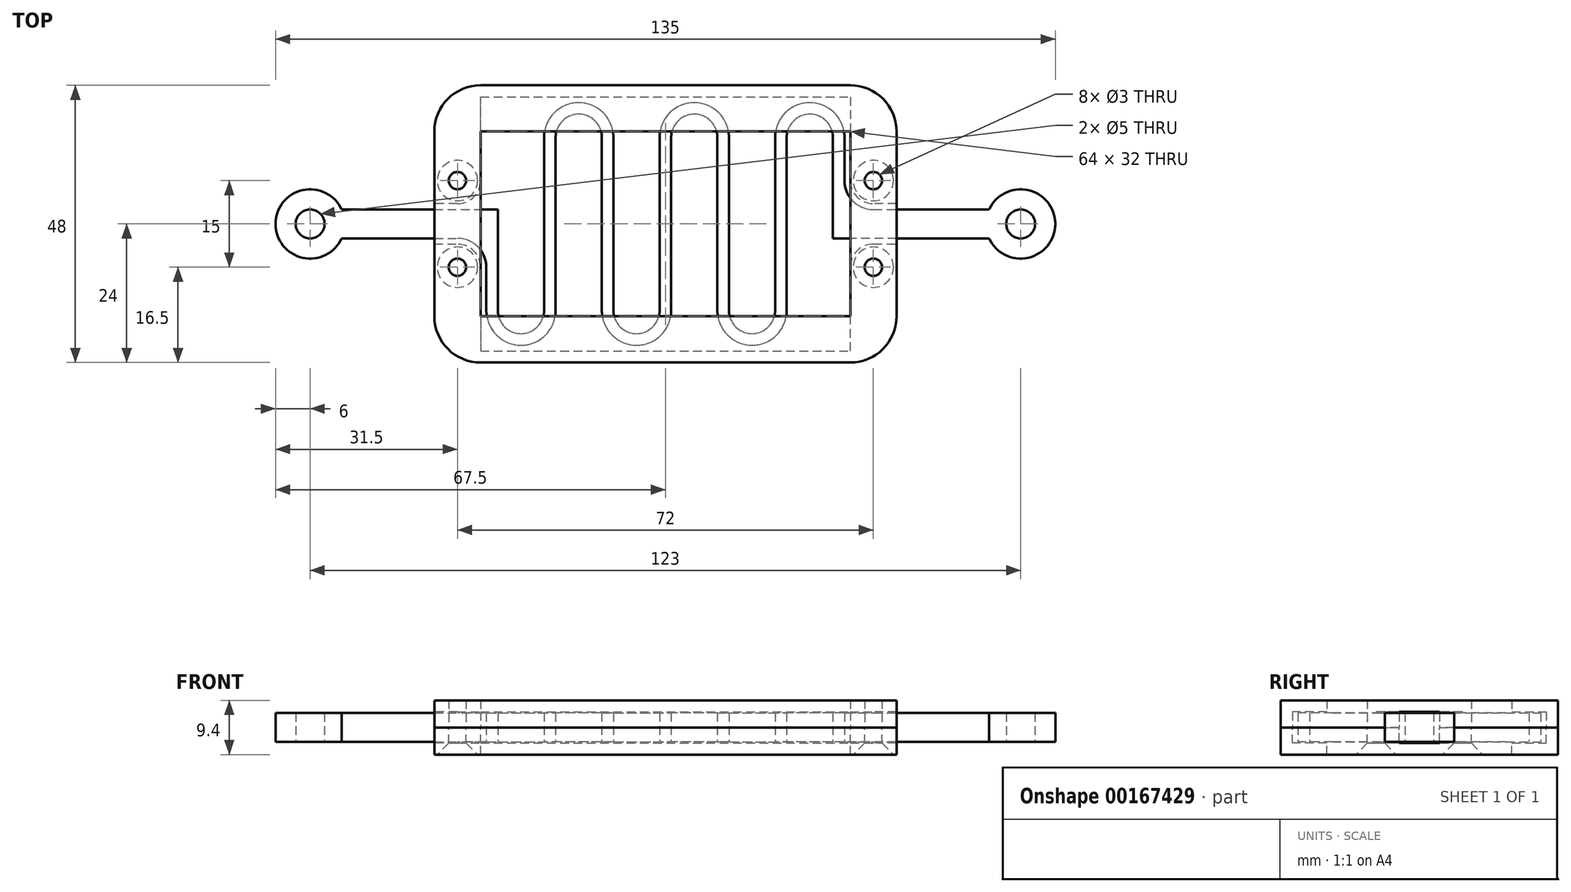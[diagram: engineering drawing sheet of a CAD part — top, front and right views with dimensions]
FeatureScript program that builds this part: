
annotation { "Feature Type Name" : "Feature", "Feature Type Description" : "" }
export const myFeature = defineFeature(function(context is Context, id is Id, definition is map)
    precondition{}
    {
        {
            var Q0;
            Q0=qCreatedBy(makeId("Top.planeOp"),FACE);
            var sketch = newSketch(context, id + "F0", { "sketchPlane" : qUnion([Q0])});
            skLineSegment(sketch, "E0", {"start": v(0, -15) * mm, "end": v(0, 15) * mm, "construction": true});
            skArc(sketch, "E1", {"start": v(10, 15) * mm, "mid": v(5, 20) * mm, "end": v(0, 15) * mm, "construction": true});
            skArc(sketch, "E2", {"start": v(-10, -15) * mm, "mid": v(-5, -20) * mm, "end": v(0, -15) * mm, "construction": true});
            skLineSegment(sketch, "E3", {"start": v(10, 15) * mm, "end": v(10, -15) * mm, "construction": true});
            skLineSegment(sketch, "E4.1.0.0", {"start": v(20, -15) * mm, "end": v(20, 15) * mm, "construction": true});
            skArc(sketch, "E4.1.0.1", {"start": v(10, -15) * mm, "mid": v(15, -20) * mm, "end": v(20, -15) * mm, "construction": true});
            skArc(sketch, "E4.1.0.2", {"start": v(30, 15) * mm, "mid": v(25, 20) * mm, "end": v(20, 15) * mm, "construction": true});
            skLineSegment(sketch, "E4.1.0.3", {"start": v(30, 15) * mm, "end": v(30, -15) * mm, "construction": true});
            skLineSegment(sketch, "E4.2.0.0", {"start": v(40, -15) * mm, "end": v(40, 15) * mm, "construction": true});
            skArc(sketch, "E4.2.0.1", {"start": v(30, -15) * mm, "mid": v(35, -20) * mm, "end": v(40, -15) * mm, "construction": true});
            skArc(sketch, "E4.2.0.2", {"start": v(50, 15) * mm, "mid": v(45, 20) * mm, "end": v(40, 15) * mm, "construction": true});
            skLineSegment(sketch, "E4.2.0.3", {"start": v(50, 15) * mm, "end": v(50, -15) * mm, "construction": true});
            skLineSegment(sketch, "E4.direction1", {"start": v(-10, -15) * mm, "end": v(10, -15) * mm, "construction": true});
            skLineSegment(sketch, "E5.bottom", {"start": v(-39, 2.5) * mm, "end": v(-9, 2.5) * mm, "construction": true});
            skLineSegment(sketch, "E5.top", {"start": v(-39, -2.5) * mm, "end": v(-16, -2.5) * mm, "construction": true});
            skLineSegment(sketch, "E5.left", {"start": v(-39, 2.5) * mm, "end": v(-39, -2.5) * mm, "construction": true});
            skLineSegment(sketch, "E5.right", {"start": v(-9, 2.5) * mm, "end": v(-9, -2.5) * mm});
            skLineSegment(sketch, "E6.top", {"start": v(49, -2.5) * mm, "end": v(79, -2.5) * mm, "construction": true});
            skLineSegment(sketch, "E6.left", {"start": v(49, 2.5) * mm, "end": v(49, -2.5) * mm});
            skLineSegment(sketch, "E6.right", {"start": v(79, 2.5) * mm, "end": v(79, -2.5) * mm, "construction": true});
            skPoint(sketch, "E7", {"position": v(-9, 0) * mm});
            skLineSegment(sketch, "E8.0", {"start": v(49, 15) * mm, "end": v(49, -2.5) * mm});
            skArc(sketch, "E8.1", {"start": v(49, 15) * mm, "mid": v(45, 19) * mm, "end": v(41, 15) * mm});
            skLineSegment(sketch, "E8.2", {"start": v(9, 15) * mm, "end": v(9, -15) * mm});
            skArc(sketch, "E8.3", {"start": v(9, 15) * mm, "mid": v(5, 19) * mm, "end": v(1, 15) * mm});
            skLineSegment(sketch, "E8.4", {"start": v(1, -15) * mm, "end": v(1, 15) * mm});
            skArc(sketch, "E8.5", {"start": v(-11, -15) * mm, "mid": v(-5, -21) * mm, "end": v(1, -15) * mm});
            skArc(sketch, "E8.6", {"start": v(9, -15) * mm, "mid": v(15, -21) * mm, "end": v(21, -15) * mm});
            skLineSegment(sketch, "E8.7", {"start": v(21, -15) * mm, "end": v(21, 15) * mm});
            skArc(sketch, "E8.8", {"start": v(29, 15) * mm, "mid": v(25, 19) * mm, "end": v(21, 15) * mm});
            skLineSegment(sketch, "E8.9", {"start": v(29, 15) * mm, "end": v(29, -15) * mm});
            skArc(sketch, "E8.10", {"start": v(29, -15) * mm, "mid": v(35, -21) * mm, "end": v(41, -15) * mm});
            skLineSegment(sketch, "E8.11", {"start": v(41, -15) * mm, "end": v(41, 15) * mm});
            skLineSegment(sketch, "E9.0", {"start": v(51, 15) * mm, "end": v(51, 7.5) * mm});
            skArc(sketch, "E9.1", {"start": v(51, 15) * mm, "mid": v(45, 21) * mm, "end": v(39, 15) * mm});
            skLineSegment(sketch, "E9.2", {"start": v(11, 15) * mm, "end": v(11, -15) * mm});
            skArc(sketch, "E9.3", {"start": v(11, 15) * mm, "mid": v(5, 21) * mm, "end": v(-1, 15) * mm});
            skLineSegment(sketch, "E9.4", {"start": v(-1, -15) * mm, "end": v(-1, 15) * mm});
            skArc(sketch, "E9.5", {"start": v(-9, -15) * mm, "mid": v(-5, -19) * mm, "end": v(-1, -15) * mm});
            skArc(sketch, "E9.6", {"start": v(11, -15) * mm, "mid": v(15, -19) * mm, "end": v(19, -15) * mm});
            skLineSegment(sketch, "E9.7", {"start": v(19, -15) * mm, "end": v(19, 15) * mm});
            skArc(sketch, "E9.8", {"start": v(31, 15) * mm, "mid": v(25, 21) * mm, "end": v(19, 15) * mm});
            skLineSegment(sketch, "E9.9", {"start": v(31, 15) * mm, "end": v(31, -15) * mm});
            skArc(sketch, "E9.10", {"start": v(31, -15) * mm, "mid": v(35, -19) * mm, "end": v(39, -15) * mm});
            skLineSegment(sketch, "E9.11", {"start": v(39, -15) * mm, "end": v(39, 15) * mm});
            skLineSegment(sketch, "E10", {"start": v(-11, -15) * mm, "end": v(-11, -7.5) * mm});
            skLineSegment(sketch, "E11", {"start": v(-9, -2.5) * mm, "end": v(-9, -15) * mm});
            skLineSegment(sketch, "E12.trimOffspring", {"start": v(56, 2.5) * mm, "end": v(79, 2.5) * mm, "construction": true});
            skPoint(sketch, "E13.visualSharp", {"position": v(-11, -2.5) * mm});
            skArc(sketch, "E13.filletArc", {"start": v(-11, -7.5) * mm, "mid": v(-12.46, -3.96) * mm, "end": v(-16, -2.5) * mm});
            skPoint(sketch, "E14.visualSharp", {"position": v(51, 2.5) * mm});
            skArc(sketch, "E14.filletArc", {"start": v(51, 7.5) * mm, "mid": v(52.46, 3.96) * mm, "end": v(56, 2.5) * mm});
            skCircle(sketch, "E15", {"center": v(-41.5, 0) * mm, "radius": 2.5 * mm});
            skArc(sketch, "E16", {"start": v(-36.05, 2.5) * mm, "mid": v(-47.5, 0) * mm, "end": v(-36.05, -2.5) * mm});
            skLineSegment(sketch, "E17", {"start": v(-36.05, 2.5) * mm, "end": v(-9, 2.5) * mm});
            skLineSegment(sketch, "E18", {"start": v(-36.05, -2.5) * mm, "end": v(-16, -2.5) * mm});
            skCircle(sketch, "E19", {"center": v(81.5, 0) * mm, "radius": 2.5 * mm});
            skArc(sketch, "E20", {"start": v(76.05, -2.5) * mm, "mid": v(87.5, 0) * mm, "end": v(76.05, 2.5) * mm});
            skLineSegment(sketch, "E21", {"start": v(56, 2.5) * mm, "end": v(76.05, 2.5) * mm});
            skLineSegment(sketch, "E22", {"start": v(76.05, -2.5) * mm, "end": v(49, -2.5) * mm});
            skSolve(sketch);
        }
        {
            var Q0;
            Q0 = qSketchRegion(id + "F0", true);
            extrude(context, id + "F1", {"entities" : qUnion([Q0]), "endBound" : BoundingType.SYMMETRIC, "depth" : 5 * mm});
        }
        {
            var Q0;
            Q0=qCreatedBy(makeId("Top.planeOp"),FACE);
            var sketch = newSketch(context, id + "F2", { "sketchPlane" : qUnion([Q0])});
            skLineSegment(sketch, "E23.bottom", {"start": v(-16, -7.5) * mm, "end": v(56, -7.5) * mm, "construction": true});
            skLineSegment(sketch, "E23.top", {"start": v(-16, 7.5) * mm, "end": v(56, 7.5) * mm, "construction": true});
            skLineSegment(sketch, "E23.left", {"start": v(-16, -7.5) * mm, "end": v(-16, 7.5) * mm, "construction": true});
            skLineSegment(sketch, "E23.right", {"start": v(56, -7.5) * mm, "end": v(56, 7.5) * mm, "construction": true});
            skCircle(sketch, "E24", {"center": v(-16, 7.5) * mm, "radius": 4 * mm, "construction": true});
            skCircle(sketch, "E25", {"center": v(-16, -7.5) * mm, "radius": 4 * mm, "construction": true});
            skCircle(sketch, "E26", {"center": v(56, -7.5) * mm, "radius": 4 * mm, "construction": true});
            skCircle(sketch, "E27", {"center": v(56, 7.5) * mm, "radius": 4 * mm, "construction": true});
            skLineSegment(sketch, "E28", {"start": v(-12, 7.5) * mm, "end": v(-12, 22) * mm});
            skLineSegment(sketch, "E29", {"start": v(-12, 22) * mm, "end": v(52, 22) * mm});
            skLineSegment(sketch, "E30", {"start": v(52, 22) * mm, "end": v(52, 7.5) * mm});
            skArc(sketch, "E31", {"start": v(-16, 3.5) * mm, "mid": v(-13.17, 4.67) * mm, "end": v(-12, 7.5) * mm});
            skArc(sketch, "E32", {"start": v(-12, -7.5) * mm, "mid": v(-13.17, -4.67) * mm, "end": v(-16, -3.5) * mm});
            skArc(sketch, "E33", {"start": v(52, 7.5) * mm, "mid": v(53.17, 4.67) * mm, "end": v(56, 3.5) * mm});
            skArc(sketch, "E34", {"start": v(56, -3.5) * mm, "mid": v(53.17, -4.67) * mm, "end": v(52, -7.5) * mm});
            skLineSegment(sketch, "E35", {"start": v(-12, -7.5) * mm, "end": v(-12, -22) * mm});
            skLineSegment(sketch, "E36", {"start": v(-12, -22) * mm, "end": v(52, -22) * mm});
            skLineSegment(sketch, "E37", {"start": v(52, -22) * mm, "end": v(52, -7.5) * mm});
            skLineSegment(sketch, "E38", {"start": v(-16, 3.5) * mm, "end": v(-20, 3.5) * mm});
            skLineSegment(sketch, "E39", {"start": v(-20, 3.5) * mm, "end": v(-20, 16) * mm});
            skLineSegment(sketch, "E40", {"start": v(-12, 24) * mm, "end": v(52, 24) * mm});
            skLineSegment(sketch, "E41", {"start": v(60, 16) * mm, "end": v(60, 3.5) * mm});
            skLineSegment(sketch, "E42", {"start": v(60, 3.5) * mm, "end": v(56, 3.5) * mm});
            skLineSegment(sketch, "E43", {"start": v(56, -3.5) * mm, "end": v(60, -3.5) * mm});
            skLineSegment(sketch, "E44", {"start": v(60, -3.5) * mm, "end": v(60, -16) * mm});
            skLineSegment(sketch, "E45", {"start": v(52, -24) * mm, "end": v(-12, -24) * mm});
            skLineSegment(sketch, "E46", {"start": v(-20, -16) * mm, "end": v(-20, -3.5) * mm});
            skLineSegment(sketch, "E47", {"start": v(-20, -3.5) * mm, "end": v(-16, -3.5) * mm});
            skPoint(sketch, "E48.visualSharp", {"position": v(-20, 24) * mm});
            skArc(sketch, "E48.filletArc", {"start": v(-12, 24) * mm, "mid": v(-17.66, 21.66) * mm, "end": v(-20, 16) * mm});
            skPoint(sketch, "E49.visualSharp", {"position": v(60, 24) * mm});
            skArc(sketch, "E49.filletArc", {"start": v(60, 16) * mm, "mid": v(57.66, 21.66) * mm, "end": v(52, 24) * mm});
            skPoint(sketch, "E50.visualSharp", {"position": v(60, -24) * mm});
            skArc(sketch, "E50.filletArc", {"start": v(52, -24) * mm, "mid": v(57.66, -21.66) * mm, "end": v(60, -16) * mm});
            skPoint(sketch, "E51.visualSharp", {"position": v(-20, -24) * mm});
            skArc(sketch, "E51.filletArc", {"start": v(-20, -16) * mm, "mid": v(-17.66, -21.66) * mm, "end": v(-12, -24) * mm});
            skCircle(sketch, "E52", {"center": v(-16, 7.5) * mm, "radius": 1.5 * mm});
            skCircle(sketch, "E53", {"center": v(-16, -7.5) * mm, "radius": 1.5 * mm});
            skCircle(sketch, "E54", {"center": v(56, 7.5) * mm, "radius": 1.5 * mm});
            skCircle(sketch, "E55", {"center": v(56, -7.5) * mm, "radius": 1.5 * mm});
            skSolve(sketch);
        }
        {
            var Q0;
            Q0=makeQuery(id+"F2.imprint","IMPRINT",FACE,{"disambiguationData":[TD([[makeQuery(id+"F2.imprint","IMPRINT",EDGE,{"derivedFrom":sQuery(id+"F2.wireOp",EDGE,"E28")}),1.0]])]});
            var Q1;
            Q1=makeQuery(id+"F2.imprint","IMPRINT",FACE,{"disambiguationData":[TD([[makeQuery(id+"F2.imprint","IMPRINT",EDGE,{"derivedFrom":sQuery(id+"F2.wireOp",EDGE,"E32")}),1.0]])]});
            extrude(context, id + "F3", {"entities" : qUnion([Q0, Q1]), "depth" : 2.7 * mm});
        }
        {
            var Q0;
            Q0=makeQuery(id+"F3.opExtrude","CAP_FACE",FACE,{"disambiguationData":[OSD([sQuery(id+"F2.wireOp",EDGE,"E32"),sQuery(id+"F2.wireOp",EDGE,"E34"),sQuery(id+"F2.wireOp",EDGE,"E35"),sQuery(id+"F2.wireOp",EDGE,"E36"),sQuery(id+"F2.wireOp",EDGE,"E37"),sQuery(id+"F2.wireOp",EDGE,"E43"),sQuery(id+"F2.wireOp",EDGE,"E44"),sQuery(id+"F2.wireOp",EDGE,"E45"),sQuery(id+"F2.wireOp",EDGE,"E46"),sQuery(id+"F2.wireOp",EDGE,"E47"),sQuery(id+"F2.wireOp",EDGE,"E50.filletArc"),sQuery(id+"F2.wireOp",EDGE,"E51.filletArc"),sQuery(id+"F2.wireOp",EDGE,"E53"),sQuery(id+"F2.wireOp",EDGE,"E55")])],"isStart":false});
            var sketch = newSketch(context, id + "F4", { "sketchPlane" : qUnion([Q0])});
            skArc(sketch, "E56.0", {"start": v(-20, -16) * mm, "mid": v(-17.66, -21.66) * mm, "end": v(-12, -24) * mm});
            skLineSegment(sketch, "E56.1", {"start": v(52, -24) * mm, "end": v(-12, -24) * mm});
            skArc(sketch, "E56.2", {"start": v(52, -24) * mm, "mid": v(57.66, -21.66) * mm, "end": v(60, -16) * mm});
            skCircle(sketch, "E56.3", {"center": v(56, -7.5) * mm, "radius": 1.5 * mm});
            skCircle(sketch, "E56.4", {"center": v(-16, -7.5) * mm, "radius": 1.5 * mm});
            skCircle(sketch, "E56.5", {"center": v(-16, 7.5) * mm, "radius": 1.5 * mm});
            skCircle(sketch, "E56.6", {"center": v(56, 7.5) * mm, "radius": 1.5 * mm});
            skArc(sketch, "E56.7", {"start": v(60, 16) * mm, "mid": v(57.66, 21.66) * mm, "end": v(52, 24) * mm});
            skLineSegment(sketch, "E56.8", {"start": v(-12, 24) * mm, "end": v(52, 24) * mm});
            skArc(sketch, "E56.9", {"start": v(-12, 24) * mm, "mid": v(-17.66, 21.66) * mm, "end": v(-20, 16) * mm});
            skLineSegment(sketch, "E57", {"start": v(-20, 16) * mm, "end": v(-20, -16) * mm});
            skLineSegment(sketch, "E58", {"start": v(60, 16) * mm, "end": v(60, -16) * mm});
            skLineSegment(sketch, "E59.bottom", {"start": v(-12, 16) * mm, "end": v(52, 16) * mm});
            skLineSegment(sketch, "E59.top", {"start": v(-12, -16) * mm, "end": v(52, -16) * mm});
            skLineSegment(sketch, "E59.left", {"start": v(-12, 16) * mm, "end": v(-12, -16) * mm});
            skLineSegment(sketch, "E59.right", {"start": v(52, 16) * mm, "end": v(52, -16) * mm});
            skSolve(sketch);
        }
        {
            var Q0;
            Q0 = qSketchRegion(id + "F4", true);
            extrude(context, id + "F5", {"entities" : qUnion([Q0]), "operationType" : NewBodyOperationType.ADD, "depth" : 2 * mm});
        }
        {
            var Q0;
            Q0=makeQuery(id+"F3.opExtrude","SWEPT_BODY",BODY,{"disambiguationData":[OSD([sQuery(id+"F2.wireOp",EDGE,"E28"),sQuery(id+"F2.wireOp",EDGE,"E29"),sQuery(id+"F2.wireOp",EDGE,"E30"),sQuery(id+"F2.wireOp",EDGE,"E31"),sQuery(id+"F2.wireOp",EDGE,"E33"),sQuery(id+"F2.wireOp",EDGE,"E38"),sQuery(id+"F2.wireOp",EDGE,"E39"),sQuery(id+"F2.wireOp",EDGE,"E40"),sQuery(id+"F2.wireOp",EDGE,"E41"),sQuery(id+"F2.wireOp",EDGE,"E42"),sQuery(id+"F2.wireOp",EDGE,"E48.filletArc"),sQuery(id+"F2.wireOp",EDGE,"E49.filletArc"),sQuery(id+"F2.wireOp",EDGE,"E52"),sQuery(id+"F2.wireOp",EDGE,"E54")])]});
            var Q1;
            Q1=qCreatedBy(makeId("Top.planeOp"),FACE);
            mirror(context, id + "F6", {"entities" : qUnion([Q0]), "mirrorPlane" : qUnion([Q1])});
        }
        {
            var Q0;
            Q0=makeQuery(id+"F6.opPattern","COPY",EDGE,{"derivedFrom":makeQuery(id+"F5.opExtrude","CAP_EDGE",EDGE,{"disambiguationData":[OSD([sQuery(id+"F4.wireOp",EDGE,"E56.4")])],"isStart":false}),"instanceName":"1"});
            var Q1;
            Q1=makeQuery(id+"F6.opPattern","COPY",EDGE,{"derivedFrom":makeQuery(id+"F5.opExtrude","CAP_EDGE",EDGE,{"disambiguationData":[OSD([sQuery(id+"F4.wireOp",EDGE,"E56.5")])],"isStart":false}),"instanceName":"1"});
            var Q2;
            Q2=makeQuery(id+"F6.opPattern","COPY",EDGE,{"derivedFrom":makeQuery(id+"F5.opExtrude","CAP_EDGE",EDGE,{"disambiguationData":[OSD([sQuery(id+"F4.wireOp",EDGE,"E56.3")])],"isStart":false}),"instanceName":"1"});
            var Q3;
            Q3=makeQuery(id+"F6.opPattern","COPY",EDGE,{"derivedFrom":makeQuery(id+"F5.opExtrude","CAP_EDGE",EDGE,{"disambiguationData":[OSD([sQuery(id+"F4.wireOp",EDGE,"E56.6")])],"isStart":false}),"instanceName":"1"});
            chamfer(context, id + "F7", {"entities" : qUnion([Q0, Q1, Q2, Q3]), "width" : 2 * mm, "tangentPropagation" : true});
        }
    });
